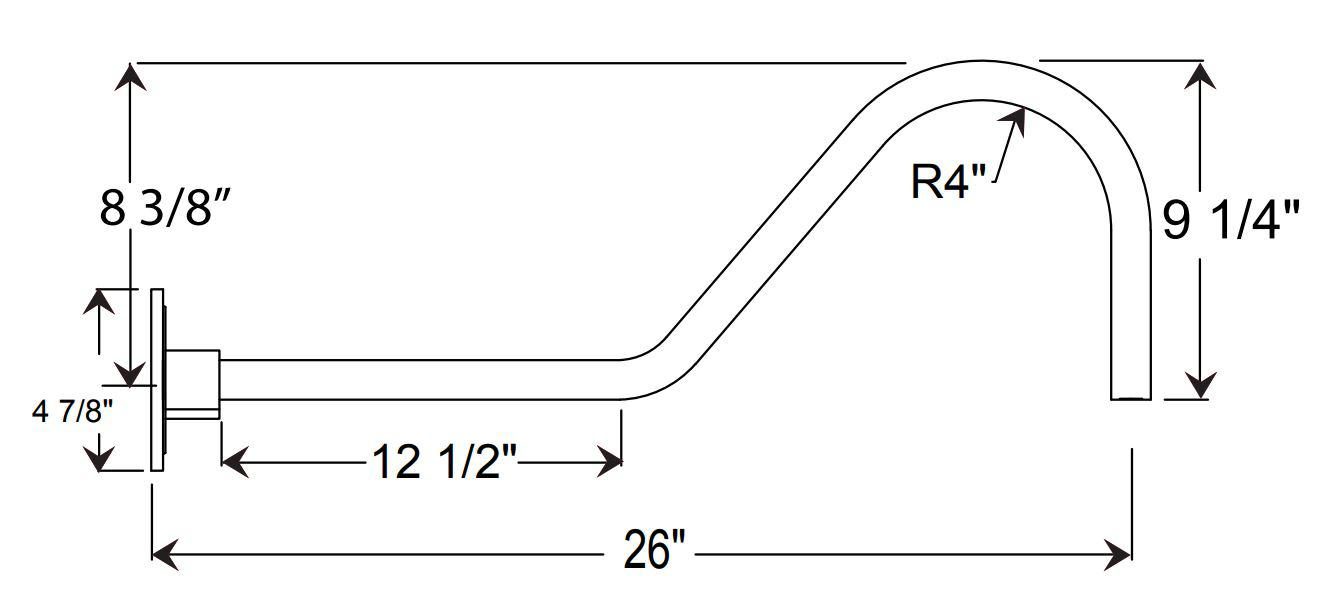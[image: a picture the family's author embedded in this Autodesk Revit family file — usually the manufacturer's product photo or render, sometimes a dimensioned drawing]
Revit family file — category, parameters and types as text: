
# Revit family: OSUL MB 16,18,38
name_source: partatom
category: Lighting Fixtures
units: mm (PartAtom-declared; Revit-internal decimal feet)

## family parameters
Always vertical = Yes
Cut with Voids When Loaded = No
Light Source = Yes
OmniClass Number = 23.80.70.00
OmniClass Title = Lighting
Part Type = Normal
Room Calculation Point = No
Round Connector Dimension = Use Diameter
Shared = No
Work Plane-Based = No

## types (3) — shared parameters
Apparent Load = 200 VA
Body Colour = Spun aluminium
Body Material = body
Bulb = Glass
CRI = >90
Canopy Body = body
Color Filter = 16777215
Construction Material = Heavy Duty spun aluminum.
Default Elevation = 0' - 0"
Description = 120-277 Voltage
Dimming = 1%
Dimming Lamp Color Temperature Shift = <None>
Efficiency = 65-125 lumens per watt
INSIDE BODY = Default
Lamp = MB
Life = L70 50,000 hours
Load Classification = Lighting
Manufacturer = ANP Lighting
Power Factor = 1
Tilt Angle = 90.00°
URL = https://www.anplighting.com
Voltage = 120 V
Warranty = 5 year limited warranty
Wattage Comments = 200 W Max
b = 0' - 2"

## per-type parameters (varying)
| type | Fixture Diameter | Fixture Height | OSUL38 | Photometric Web File | UL 416 | UL 418 | Weight | a |
| OSUL38 | 3' - 2" | 2' - 11" | Yes | OSUL38M037LDNW40K.IES | No | No | 12.0 lbs | 2' - 4" |
| UL418 | 1' - 6" | 1' - 4 1/2" | No | generic | No | Yes | 2.5lbs | 1' - 6" |
| UL416 | 1' - 4 1/4" | 1' - 2 1/2" | No | UL416-100W-INC.-T15293t.IES | Yes | No | 1.5lbs | 1' - 2" |

note: column(s) folded — value = type name in every type: Model

## geometry (parser evidence)
native form markers: Sweep x34
no freeform markers — native parametric forms only
